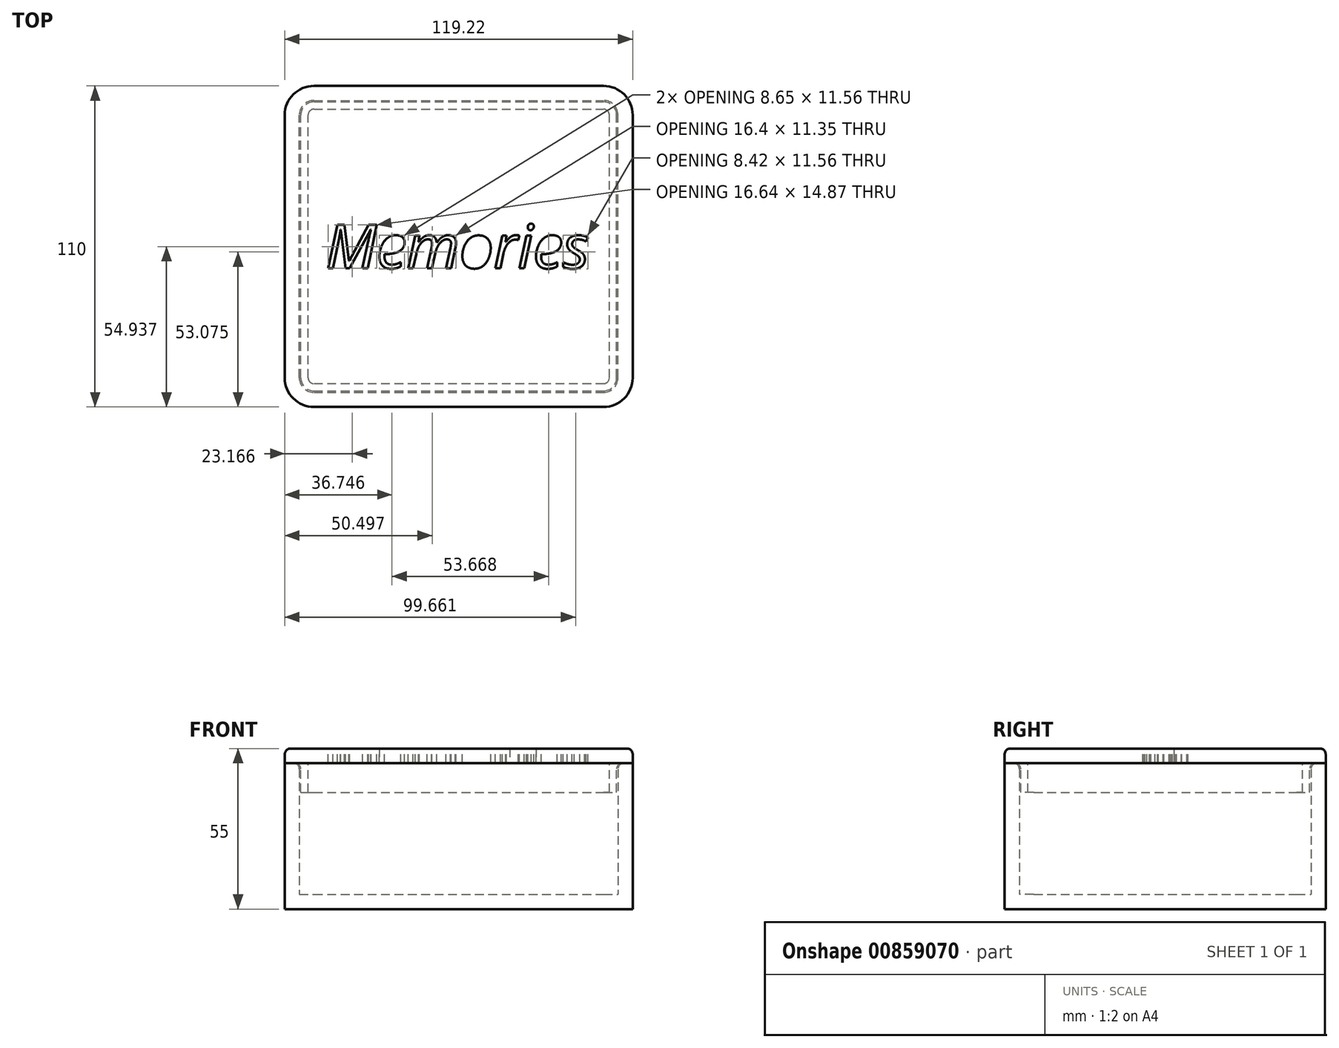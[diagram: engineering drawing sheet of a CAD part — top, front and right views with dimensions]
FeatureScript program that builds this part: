
annotation { "Feature Type Name" : "Feature", "Feature Type Description" : "" }
export const myFeature = defineFeature(function(context is Context, id is Id, definition is map)
    precondition{}
    {
        {
            var Q0;
            Q0=qCreatedBy(makeId("Top.planeOp"),FACE);
            var sketch = newSketch(context, id + "F0", { "sketchPlane" : qUnion([Q0])});
            skLineSegment(sketch, "E0.bottom", {"start": v(-54.6, -50) * mm, "end": v(54.61, -50) * mm});
            skLineSegment(sketch, "E0.top", {"start": v(-54.61, 50) * mm, "end": v(54.6, 50) * mm});
            skLineSegment(sketch, "E0.left", {"start": v(-54.6, -50) * mm, "end": v(-54.61, 50) * mm});
            skLineSegment(sketch, "E0.right", {"start": v(54.61, -50) * mm, "end": v(54.6, 50) * mm});
            skPoint(sketch, "E0.middle", {"position": v(0, 0) * mm});
            skLineSegment(sketch, "E1.0", {"start": v(-59.61, 55) * mm, "end": v(59.6, 55) * mm});
            skLineSegment(sketch, "E1.1", {"start": v(-59.6, -55) * mm, "end": v(-59.61, 55) * mm});
            skLineSegment(sketch, "E1.2", {"start": v(-59.6, -55) * mm, "end": v(59.61, -55) * mm});
            skLineSegment(sketch, "E1.3", {"start": v(59.61, -55) * mm, "end": v(59.6, 55) * mm});
            skLineSegment(sketch, "E2.bottom", {"start": v(-53.97, -44) * mm, "end": v(53.98, -44) * mm, "construction": true});
            skLineSegment(sketch, "E2.top", {"start": v(-53.98, 44) * mm, "end": v(53.97, 44) * mm, "construction": true});
            skLineSegment(sketch, "E2.left", {"start": v(-53.98, -44) * mm, "end": v(-53.98, 44) * mm, "construction": true});
            skLineSegment(sketch, "E2.right", {"start": v(53.98, -44) * mm, "end": v(53.98, 44) * mm, "construction": true});
            skSolve(sketch);
        }
        {
            var Q0;
            Q0 = qSketchRegion(id + "F0", true);
            var Q1;
            Q1=makeQuery(id+"F0.imprint","IMPRINT",FACE,{"disambiguationData":[TD([[makeQuery(id+"F0.imprint","IMPRINT",EDGE,{"derivedFrom":sQuery(id+"F0.wireOp",EDGE,"E0.bottom")}),1.0]])]});
            extrude(context, id + "F1", {"entities" : qUnion([Q0, Q1]), "oppositeDirection" : true, "depth" : 5 * mm, "offsetDistance" : 25 * mm});
        }
        {
            var Q0;
            Q0=makeQuery(id+"F0.imprint","IMPRINT",FACE,{"disambiguationData":[TD([[makeQuery(id+"F0.imprint","IMPRINT",EDGE,{"derivedFrom":sQuery(id+"F0.wireOp",EDGE,"E0.bottom")}),-1.0]])]});
            extrude(context, id + "F2", {"entities" : qUnion([Q0]), "operationType" : NewBodyOperationType.ADD, "depth" : 45 * mm, "offsetDistance" : 25 * mm});
        }
        {
            var Q0;
            Q0=makeQuery(id+"F2.opExtrude","SWEPT_EDGE",EDGE,{"disambiguationData":[OSD([sQuery(id+"F0.wireOp",EDGE,"E0.top"),sQuery(id+"F0.wireOp",EDGE,"E0.left")])]});
            var Q1;
            Q1=makeQuery(id+"F2.opExtrude","SWEPT_EDGE",EDGE,{"disambiguationData":[OSD([sQuery(id+"F0.wireOp",EDGE,"E0.top"),sQuery(id+"F0.wireOp",EDGE,"E0.right")])]});
            var Q2;
            Q2=makeQuery(id+"F2.opExtrude","SWEPT_EDGE",EDGE,{"disambiguationData":[OSD([sQuery(id+"F0.wireOp",EDGE,"E0.bottom"),sQuery(id+"F0.wireOp",EDGE,"E0.right")])]});
            var Q3;
            Q3=makeQuery(id+"F2.opExtrude","SWEPT_EDGE",EDGE,{"disambiguationData":[OSD([sQuery(id+"F0.wireOp",EDGE,"E0.bottom"),sQuery(id+"F0.wireOp",EDGE,"E0.left")])]});
            fillet(context, id + "F3", {"entities" : qUnion([Q0, Q1, Q2, Q3]), "radius" : 5 * mm, "tangentPropagation" : true, "allowEdgeOverflow" : false});
        }
        {
            var Q0;
            {var subQ0=sQuery(id+"F0.wireOp",EDGE,"E1.2");var subQ1=sQuery(id+"F0.wireOp",EDGE,"E1.1");Q0=makeQuery(id+"F2.boolean.opBoolean","MERGE",EDGE,{"derivedFrom":[makeQuery(id+"F1.opExtrude","SWEPT_EDGE",EDGE,{"disambiguationData":[OSD([subQ1,subQ0])]}),makeQuery(id+"F2.opExtrude","SWEPT_EDGE",EDGE,{"disambiguationData":[OSD([subQ1,subQ0])]})]});}
            var Q1;
            {var subQ0=sQuery(id+"F0.wireOp",EDGE,"E1.3");var subQ1=sQuery(id+"F0.wireOp",EDGE,"E1.2");Q1=makeQuery(id+"F2.boolean.opBoolean","MERGE",EDGE,{"derivedFrom":[makeQuery(id+"F1.opExtrude","SWEPT_EDGE",EDGE,{"disambiguationData":[OSD([subQ1,subQ0])]}),makeQuery(id+"F2.opExtrude","SWEPT_EDGE",EDGE,{"disambiguationData":[OSD([subQ1,subQ0])]})]});}
            var Q2;
            {var subQ0=sQuery(id+"F0.wireOp",EDGE,"E1.3");var subQ1=sQuery(id+"F0.wireOp",EDGE,"E1.0");Q2=makeQuery(id+"F2.boolean.opBoolean","MERGE",EDGE,{"derivedFrom":[makeQuery(id+"F1.opExtrude","SWEPT_EDGE",EDGE,{"disambiguationData":[OSD([subQ1,subQ0])]}),makeQuery(id+"F2.opExtrude","SWEPT_EDGE",EDGE,{"disambiguationData":[OSD([subQ1,subQ0])]})]});}
            var Q3;
            {var subQ0=sQuery(id+"F0.wireOp",EDGE,"E1.1");var subQ1=sQuery(id+"F0.wireOp",EDGE,"E1.0");Q3=makeQuery(id+"F2.boolean.opBoolean","MERGE",EDGE,{"derivedFrom":[makeQuery(id+"F1.opExtrude","SWEPT_EDGE",EDGE,{"disambiguationData":[OSD([subQ1,subQ0])]}),makeQuery(id+"F2.opExtrude","SWEPT_EDGE",EDGE,{"disambiguationData":[OSD([subQ1,subQ0])]})]});}
            fillet(context, id + "F4", {"entities" : qUnion([Q0, Q1, Q2, Q3]), "radius" : 10 * mm, "tangentPropagation" : true, "allowEdgeOverflow" : false});
        }
        {
            var Q0;
            Q0=makeQuery(id+"F2.opExtrude","CAP_FACE",FACE,{"disambiguationData":[OSD([sQuery(id+"F0.wireOp",EDGE,"E0.bottom"),sQuery(id+"F0.wireOp",EDGE,"E0.top"),sQuery(id+"F0.wireOp",EDGE,"E0.left"),sQuery(id+"F0.wireOp",EDGE,"E0.right"),sQuery(id+"F0.wireOp",EDGE,"E1.0"),sQuery(id+"F0.wireOp",EDGE,"E1.1"),sQuery(id+"F0.wireOp",EDGE,"E1.2"),sQuery(id+"F0.wireOp",EDGE,"E1.3")])],"isStart":false});
            var sketch = newSketch(context, id + "F5", { "sketchPlane" : qUnion([Q0])});
            skLineSegment(sketch, "E3.0", {"start": v(-54.11, -45) * mm, "end": v(-54.11, 45) * mm});
            skArc(sketch, "E3.1", {"start": v(-49.6, -49.5) * mm, "mid": v(-52.8, -48.18) * mm, "end": v(-54.11, -45) * mm});
            skArc(sketch, "E3.2", {"start": v(-54.11, 45) * mm, "mid": v(-52.8, 48.18) * mm, "end": v(-49.61, 49.5) * mm});
            skLineSegment(sketch, "E3.3", {"start": v(-49.6, -49.5) * mm, "end": v(49.6, -49.5) * mm});
            skLineSegment(sketch, "E3.4", {"start": v(-49.61, 49.5) * mm, "end": v(49.6, 49.5) * mm});
            skArc(sketch, "E3.5", {"start": v(49.6, 49.5) * mm, "mid": v(52.8, 48.18) * mm, "end": v(54.11, 45) * mm});
            skLineSegment(sketch, "E3.6", {"start": v(54.11, -45) * mm, "end": v(54.11, 45) * mm});
            skArc(sketch, "E3.7", {"start": v(54.11, -45) * mm, "mid": v(52.8, -48.18) * mm, "end": v(49.61, -49.5) * mm});
            skLineSegment(sketch, "E4.0", {"start": v(-51.61, -45) * mm, "end": v(-51.61, 45) * mm});
            skArc(sketch, "E4.1", {"start": v(-49.6, -47) * mm, "mid": v(-51.02, -46.41) * mm, "end": v(-51.61, -45) * mm});
            skArc(sketch, "E4.2", {"start": v(-51.61, 45) * mm, "mid": v(-51.02, 46.41) * mm, "end": v(-49.61, 47) * mm});
            skLineSegment(sketch, "E4.3", {"start": v(-49.6, -47) * mm, "end": v(49.6, -47) * mm});
            skLineSegment(sketch, "E4.4", {"start": v(-49.61, 47) * mm, "end": v(49.6, 47) * mm});
            skArc(sketch, "E4.5", {"start": v(49.6, 47) * mm, "mid": v(51.02, 46.41) * mm, "end": v(51.61, 45) * mm});
            skLineSegment(sketch, "E4.6", {"start": v(51.61, -45) * mm, "end": v(51.61, 45) * mm});
            skArc(sketch, "E4.7", {"start": v(51.61, -45) * mm, "mid": v(51.02, -46.41) * mm, "end": v(49.61, -47) * mm});
            skArc(sketch, "E5.0", {"start": v(-59.61, -45) * mm, "mid": v(-56.68, -52.07) * mm, "end": v(-49.6, -55) * mm});
            skLineSegment(sketch, "E5.1", {"start": v(-59.61, 45) * mm, "end": v(-59.6, -45) * mm});
            skLineSegment(sketch, "E5.2", {"start": v(-49.6, -55) * mm, "end": v(49.6, -55) * mm});
            skArc(sketch, "E5.3", {"start": v(-49.61, 55) * mm, "mid": v(-56.68, 52.07) * mm, "end": v(-59.61, 45) * mm});
            skArc(sketch, "E5.4", {"start": v(49.61, -55) * mm, "mid": v(56.68, -52.07) * mm, "end": v(59.61, -45) * mm});
            skLineSegment(sketch, "E5.5", {"start": v(59.61, -45) * mm, "end": v(59.6, 45) * mm});
            skArc(sketch, "E5.6", {"start": v(59.61, 45) * mm, "mid": v(56.68, 52.07) * mm, "end": v(49.6, 55) * mm});
            skLineSegment(sketch, "E5.7", {"start": v(49.6, 55) * mm, "end": v(-49.61, 55) * mm});
            skSolve(sketch);
        }
        {
            var Q0;
            Q0=makeQuery(id+"F5.imprint","IMPRINT",FACE,{"disambiguationData":[TD([[makeQuery(id+"F5.imprint","IMPRINT",EDGE,{"derivedFrom":sQuery(id+"F5.wireOp",EDGE,"E5.0")}),1.0]])]});
            var Q1;
            {var subQ5=sQuery(id+"F0.wireOp",EDGE,"E0.bottom");Q1=makeQuery(id+"F5.imprint","IMPRINT",FACE,{"disambiguationData":[TD([[makeQuery(id+"F5.imprint","IMPRINT",EDGE,{"derivedFrom":makeQuery(id+"F2.opExtrude","CAP_EDGE",EDGE,{"disambiguationData":[OSD([subQ5])],"isStart":false})}),-1.0]])]});}
            var Q2;
            Q2=makeQuery(id+"F5.imprint","IMPRINT",FACE,{"disambiguationData":[TD([[makeQuery(id+"F5.imprint","IMPRINT",EDGE,{"derivedFrom":sQuery(id+"F5.wireOp",EDGE,"E4.0")}),-1.0]])]});
            var Q3;
            Q3=makeQuery(id+"F5.imprint","IMPRINT",FACE,{"disambiguationData":[TD([[makeQuery(id+"F5.imprint","IMPRINT",EDGE,{"derivedFrom":sQuery(id+"F5.wireOp",EDGE,"E3.0")}),1.0]])]});
            var Q4;
            Q4=makeQuery(id+"F5.imprint","IMPRINT",FACE,{"disambiguationData":[TD([[makeQuery(id+"F5.imprint","IMPRINT",EDGE,{"derivedFrom":sQuery(id+"F5.wireOp",EDGE,"E3.0")}),-1.0]])]});
            extrude(context, id + "F6", {"entities" : qUnion([Q0, Q1, Q2, Q3, Q4]), "depth" : 5 * mm, "offsetDistance" : 25 * mm});
        }
        {
            var Q0;
            Q0=makeQuery(id+"F5.imprint","IMPRINT",FACE,{"disambiguationData":[TD([[makeQuery(id+"F5.imprint","IMPRINT",EDGE,{"derivedFrom":sQuery(id+"F5.wireOp",EDGE,"E3.0")}),-1.0]])]});
            extrude(context, id + "F7", {"entities" : qUnion([Q0]), "operationType" : NewBodyOperationType.ADD, "oppositeDirection" : true, "depth" : 10 * mm, "offsetDistance" : 25 * mm});
        }
        {
            var Q0;
            Q0=makeQuery(id+"F2.opExtrude","CAP_EDGE",EDGE,{"disambiguationData":[OSD([sQuery(id+"F0.wireOp",EDGE,"E0.left")])],"isStart":false});
            var Q1;
            Q1=makeQuery(id+"F7.opExtrude","CAP_EDGE",EDGE,{"disambiguationData":[OSD([sQuery(id+"F5.wireOp",EDGE,"E3.0")])],"isStart":true});
            var Q2;
            Q2=makeQuery(id+"F7.opExtrude","CAP_EDGE",EDGE,{"disambiguationData":[OSD([sQuery(id+"F5.wireOp",EDGE,"E4.0")])],"isStart":true});
            fillet(context, id + "F8", {"entities" : qUnion([Q0, Q1, Q2]), "radius" : 2 * mm, "tangentPropagation" : true, "allowEdgeOverflow" : false});
        }
        {
            var Q0;
            Q0=makeQuery(id+"F6.opExtrude","CAP_FACE",FACE,{"disambiguationData":[OSD([sQuery(id+"F5.wireOp",EDGE,"E5.0"),sQuery(id+"F5.wireOp",EDGE,"E5.1"),sQuery(id+"F5.wireOp",EDGE,"E5.2"),sQuery(id+"F5.wireOp",EDGE,"E5.3"),sQuery(id+"F5.wireOp",EDGE,"E5.4"),sQuery(id+"F5.wireOp",EDGE,"E5.5"),sQuery(id+"F5.wireOp",EDGE,"E5.6"),sQuery(id+"F5.wireOp",EDGE,"E5.7")])],"isStart":false});
            var sketch = newSketch(context, id + "F9", { "sketchPlane" : qUnion([Q0])});
            skText(sketch, "E6", { "text": "Memories", "fontName": "OpenSans-Italic.ttf"});
            skPoint(sketch, "E7", {"position": v(0, 0) * mm});
            const initialGuessF9  = {"E6": [-0.04562, -0.0075, 1, 0, 0.015]};
            skSetInitialGuess(sketch, initialGuessF9);
            skSolve(sketch);
        }
        {
            var Q0;
            Q0 = qSketchRegion(id + "F9", true);
            var Q1;
            Q1=makeQuery(id+"F9.imprint","IMPRINT",FACE,{"disambiguationData":[TD([[makeQuery(id+"F9.imprint","IMPRINT",EDGE,{"derivedFrom":sQuery(id+"F9.wireOp",EDGE,"E6.sketch_text.stroke-37")}),1.0]])]});
            var Q2;
            Q2=makeQuery(id+"F9.imprint","IMPRINT",FACE,{"disambiguationData":[TD([[makeQuery(id+"F9.imprint","IMPRINT",EDGE,{"derivedFrom":sQuery(id+"F9.wireOp",EDGE,"E6.sketch_text.stroke-88")}),1.0]])]});
            var Q3;
            Q3=makeQuery(id+"F9.imprint","IMPRINT",FACE,{"disambiguationData":[TD([[makeQuery(id+"F9.imprint","IMPRINT",EDGE,{"derivedFrom":sQuery(id+"F9.wireOp",EDGE,"E6.sketch_text.stroke-142")}),1.0]])]});
            extrude(context, id + "F10", {"entities" : qUnion([Q0, Q1, Q2, Q3]), "operationType" : NewBodyOperationType.REMOVE, "oppositeDirection" : true, "depth" : 25 * mm, "offsetDistance" : 25 * mm});
        }
        {
            var Q0;
            Q0=makeQuery(id+"F6.opExtrude","CAP_EDGE",EDGE,{"disambiguationData":[OSD([sQuery(id+"F5.wireOp",EDGE,"E5.1")])],"isStart":false});
            fillet(context, id + "F11", {"entities" : qUnion([Q0]), "radius" : 2 * mm, "tangentPropagation" : true, "allowEdgeOverflow" : false});
        }
    });
